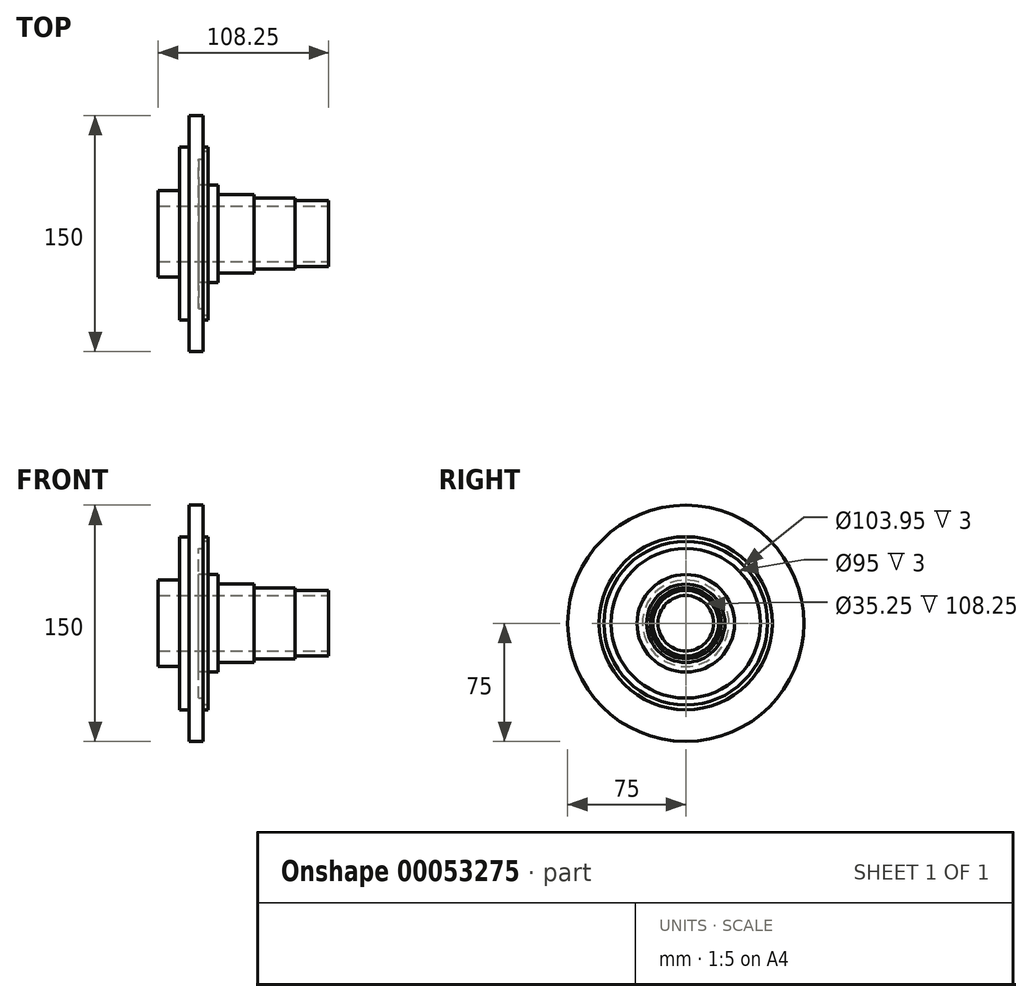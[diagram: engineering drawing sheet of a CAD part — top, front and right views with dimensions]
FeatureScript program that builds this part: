
annotation { "Feature Type Name" : "Feature", "Feature Type Description" : "" }
export const myFeature = defineFeature(function(context is Context, id is Id, definition is map)
    precondition{}
    {
        {
            var Q0;
            Q0=qCreatedBy(makeId("Right.planeOp"),FACE);
            var sketch = newSketch(context, id + "F0", { "sketchPlane" : qUnion([Q0])});
            skCircle(sketch, "E0", {"center": v(0, 0) * mm, "radius": 75 * mm});
            skSolve(sketch);
        }
        {
            var Q0;
            Q0 = qSketchRegion(id + "F0", true);
            extrude(context, id + "F1", {"entities" : qUnion([Q0]), "depth" : 9 * mm});
        }
        {
            var Q0;
            Q0=makeQuery(id+"F1.opExtrude","CAP_FACE",FACE,{"disambiguationData":[OSD([sQuery(id+"F0.wireOp",EDGE,"E0")])],"isStart":false});
            var sketch = newSketch(context, id + "F2", { "sketchPlane" : qUnion([Q0])});
            skCircle(sketch, "E1", {"center": v(0, 0) * mm, "radius": 51.98 * mm});
            skCircle(sketch, "E2", {"center": v(0, 0) * mm, "radius": 54.98 * mm});
            skSolve(sketch);
        }
        {
            var Q0;
            Q0=makeQuery(id+"F2.imprint","IMPRINT",FACE,{"disambiguationData":[TD([[makeQuery(id+"F2.imprint","IMPRINT",EDGE,{"derivedFrom":sQuery(id+"F2.wireOp",EDGE,"E1")}),-1.0]])]});
            extrude(context, id + "F3", {"entities" : qUnion([Q0]), "operationType" : NewBodyOperationType.ADD, "depth" : 3 * mm});
        }
        {
            var Q0;
            Q0=makeQuery(id+"F3.boolean.opBoolean","SPLIT",FACE,{"disambiguationData":[TD([makeQuery(id+"F3.opExtrude","SWEPT_FACE",FACE,{"disambiguationData":[OSD([sQuery(id+"F2.wireOp",EDGE,"E1")])]})])],"derivedFrom":makeQuery(id+"F1.opExtrude","CAP_FACE",FACE,{"disambiguationData":[OSD([sQuery(id+"F0.wireOp",EDGE,"E0")])],"isStart":false})});
            var sketch = newSketch(context, id + "F4", { "sketchPlane" : qUnion([Q0])});
            skCircle(sketch, "E3", {"center": v(0, 0) * mm, "radius": 47.5 * mm});
            skSolve(sketch);
        }
        {
            var Q0;
            Q0 = qSketchRegion(id + "F4", true);
            extrude(context, id + "F5", {"entities" : qUnion([Q0]), "operationType" : NewBodyOperationType.REMOVE, "oppositeDirection" : true, "depth" : 3 * mm});
        }
        {
            var Q0;
            Q0=makeQuery(id+"F1.opExtrude","CAP_FACE",FACE,{"disambiguationData":[OSD([sQuery(id+"F0.wireOp",EDGE,"E0")])],"isStart":true});
            var sketch = newSketch(context, id + "F6", { "sketchPlane" : qUnion([Q0])});
            skCircle(sketch, "E4", {"center": v(0, 0) * mm, "radius": 54.98 * mm});
            skSolve(sketch);
        }
        {
            var Q0;
            Q0 = qSketchRegion(id + "F6", true);
            extrude(context, id + "F7", {"entities" : qUnion([Q0]), "operationType" : NewBodyOperationType.ADD, "depth" : 6 * mm});
        }
        {
            var Q0;
            Q0=makeQuery(id+"F5.boolean.opBoolean","COPY",FACE,{"derivedFrom":makeQuery(id+"F5.opExtrude","CAP_FACE",FACE,{"disambiguationData":[OSD([sQuery(id+"F4.wireOp",EDGE,"E3")])],"isStart":false})});
            var sketch = newSketch(context, id + "F8", { "sketchPlane" : qUnion([Q0])});
            skCircle(sketch, "E5", {"center": v(0, 0) * mm, "radius": 30.97 * mm});
            skSolve(sketch);
        }
        {
            var Q0;
            Q0 = qSketchRegion(id + "F8", true);
            extrude(context, id + "F9", {"entities" : qUnion([Q0]), "operationType" : NewBodyOperationType.ADD, "depth" : 12.5 * mm});
        }
        {
            var Q0;
            Q0=makeQuery(id+"F9.opExtrude","CAP_FACE",FACE,{"disambiguationData":[OSD([sQuery(id+"F8.wireOp",EDGE,"E5")])],"isStart":false});
            var sketch = newSketch(context, id + "F10", { "sketchPlane" : qUnion([Q0])});
            skCircle(sketch, "E6", {"center": v(0, 0) * mm, "radius": 24.9 * mm});
            skSolve(sketch);
        }
        {
            var Q0;
            Q0 = qSketchRegion(id + "F10", true);
            extrude(context, id + "F11", {"entities" : qUnion([Q0]), "operationType" : NewBodyOperationType.ADD, "depth" : 23 * mm});
        }
        {
            var Q0;
            Q0=makeQuery(id+"F11.opExtrude","CAP_FACE",FACE,{"disambiguationData":[OSD([sQuery(id+"F10.wireOp",EDGE,"E6")])],"isStart":false});
            var sketch = newSketch(context, id + "F12", { "sketchPlane" : qUnion([Q0])});
            skCircle(sketch, "E7", {"center": v(0, 0) * mm, "radius": 22.58 * mm});
            skSolve(sketch);
        }
        {
            var Q0;
            Q0 = qSketchRegion(id + "F12", true);
            extrude(context, id + "F13", {"entities" : qUnion([Q0]), "operationType" : NewBodyOperationType.ADD, "depth" : 26 * mm});
        }
        {
            var Q0;
            Q0=makeQuery(id+"F13.opExtrude","CAP_FACE",FACE,{"disambiguationData":[OSD([sQuery(id+"F12.wireOp",EDGE,"E7")])],"isStart":false});
            var sketch = newSketch(context, id + "F14", { "sketchPlane" : qUnion([Q0])});
            skCircle(sketch, "E8", {"center": v(0, 0) * mm, "radius": 20.88 * mm});
            skSolve(sketch);
        }
        {
            var Q0;
            Q0 = qSketchRegion(id + "F14", true);
            extrude(context, id + "F15", {"entities" : qUnion([Q0]), "operationType" : NewBodyOperationType.ADD, "depth" : 21.25 * mm});
        }
        {
            var Q0;
            Q0=makeQuery(id+"F7.opExtrude","CAP_FACE",FACE,{"disambiguationData":[OSD([sQuery(id+"F6.wireOp",EDGE,"E4")])],"isStart":false});
            var sketch = newSketch(context, id + "F16", { "sketchPlane" : qUnion([Q0])});
            skCircle(sketch, "E9", {"center": v(0, 0) * mm, "radius": 27.5 * mm});
            skSolve(sketch);
        }
        {
            var Q0;
            Q0 = qSketchRegion(id + "F16", true);
            extrude(context, id + "F17", {"entities" : qUnion([Q0]), "operationType" : NewBodyOperationType.ADD, "depth" : 13.5 * mm});
        }
        {
            var Q0;
            Q0=qCreatedBy(makeId("Right.planeOp"),FACE);
            var sketch = newSketch(context, id + "F18", { "sketchPlane" : qUnion([Q0])});
            skCircle(sketch, "E10", {"center": v(0, 0) * mm, "radius": 16.83 * mm});
            skSolve(sketch);
        }
        {
            var Q0;
            Q0 = qSketchRegion(id + "F18", true);
            extrude(context, id + "F19", {"entities" : qUnion([Q0]), "operationType" : NewBodyOperationType.REMOVE, "endBound" : BoundingType.THROUGH_ALL, "oppositeDirection" : true, "depth" : 25 * mm, "hasSecondDirection" : true, "secondDirectionBound" : SecondDirectionBoundingType.THROUGH_ALL, "secondDirectionOppositeDirection" : false, "secondDirectionDepth" : 25 * mm});
        }
        {
            var Q0;
            Q0=makeQuery(id+"F15.opExtrude","CAP_FACE",FACE,{"disambiguationData":[OSD([sQuery(id+"F14.wireOp",EDGE,"E8")])],"isStart":false});
            var sketch = newSketch(context, id + "F20", { "sketchPlane" : qUnion([Q0])});
            skCircle(sketch, "E11", {"center": v(0, 0) * mm, "radius": 17.62 * mm});
            skSolve(sketch);
        }
        {
            var Q0;
            Q0 = qSketchRegion(id + "F20", true);
            extrude(context, id + "F21", {"entities" : qUnion([Q0]), "operationType" : NewBodyOperationType.REMOVE, "oppositeDirection" : true, "depth" : 122 * mm});
        }
    });
